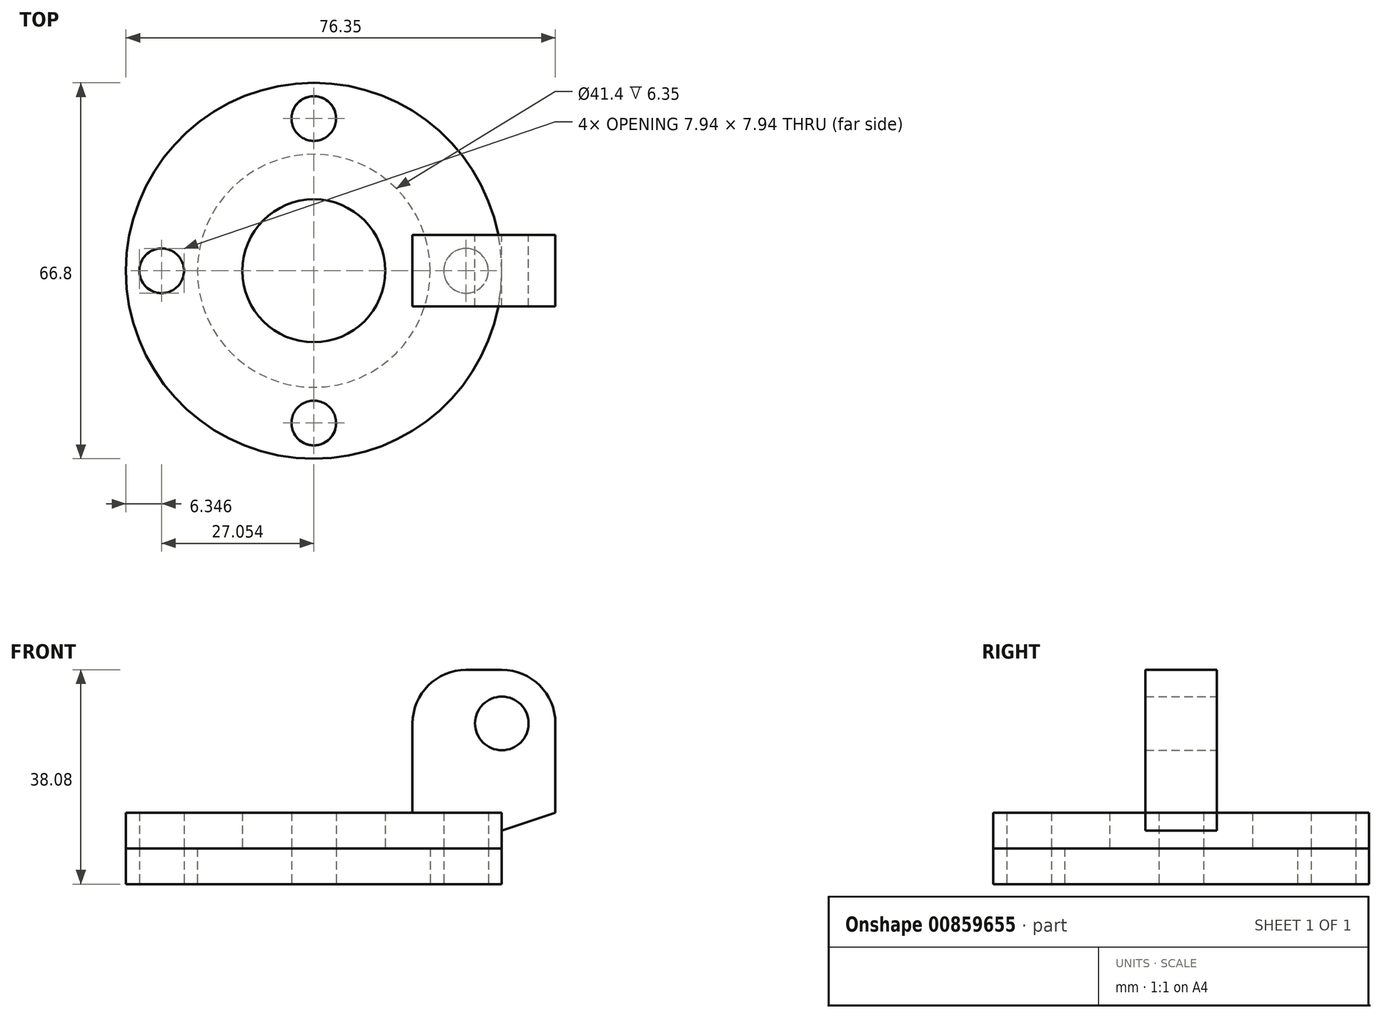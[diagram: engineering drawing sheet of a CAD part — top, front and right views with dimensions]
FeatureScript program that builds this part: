
annotation { "Feature Type Name" : "Feature", "Feature Type Description" : "" }
export const myFeature = defineFeature(function(context is Context, id is Id, definition is map)
    precondition{}
    {
        {
            var Q0;
            Q0=qCreatedBy(makeId("Top.planeOp"),FACE);
            var sketch = newSketch(context, id + "F0", { "sketchPlane" : qUnion([Q0])});
            skCircle(sketch, "E0", {"center": v(0, 0) * mm, "radius": 33.4 * mm});
            skCircle(sketch, "E1", {"center": v(0, 0) * mm, "radius": 20.7 * mm});
            skCircle(sketch, "E2", {"center": v(0, 27.05) * mm, "radius": 3.97 * mm});
            skCircle(sketch, "E3.1.0", {"center": v(-27.05, 0) * mm, "radius": 3.97 * mm});
            skCircle(sketch, "E3.2.0", {"center": v(0, -27.05) * mm, "radius": 3.97 * mm});
            skCircle(sketch, "E3.3.0", {"center": v(27.05, 0) * mm, "radius": 3.97 * mm});
            skSolve(sketch);
        }
        {
            var Q0;
            Q0=makeQuery(id+"F0.imprint","IMPRINT",FACE,{"disambiguationData":[TD([[makeQuery(id+"F0.imprint","IMPRINT",EDGE,{"derivedFrom":sQuery(id+"F0.wireOp",EDGE,"E0")}),1.0]])]});
            extrude(context, id + "F1", {"entities" : qUnion([Q0]), "endBound" : BoundingType.SYMMETRIC, "depth" : 6.35 * mm, "offsetDistance" : 25.4 * mm});
        }
        {
            var Q0;
            Q0=makeQuery(id+"F1.opExtrude","CAP_FACE",FACE,{"disambiguationData":[OSD([sQuery(id+"F0.wireOp",EDGE,"E0"),sQuery(id+"F0.wireOp",EDGE,"E1"),sQuery(id+"F0.wireOp",EDGE,"E2"),sQuery(id+"F0.wireOp",EDGE,"E3.1.0"),sQuery(id+"F0.wireOp",EDGE,"E3.2.0"),sQuery(id+"F0.wireOp",EDGE,"E3.3.0")])],"isStart":false});
            var Q1;
            Q1=qCreatedBy(makeId("Front.planeOp"),FACE);
            var Q2;
            Q2=qCreatedBy(makeId("Top.planeOp"),FACE);
            var sketch = newSketch(context, id + "F2", { "sketchPlane" : qUnion([Q0, Q1, Q2])});
            skCircle(sketch, "E4", {"center": v(0, 0) * mm, "radius": 33.4 * mm});
            skCircle(sketch, "E5", {"center": v(0, 0) * mm, "radius": 12.7 * mm});
            skCircle(sketch, "E6", {"center": v(0, 27.06) * mm, "radius": 3.97 * mm});
            skCircle(sketch, "E7", {"center": v(27.06, 0) * mm, "radius": 3.97 * mm});
            skCircle(sketch, "E8", {"center": v(0, -27.06) * mm, "radius": 3.97 * mm});
            skCircle(sketch, "E9", {"center": v(-27.06, 0) * mm, "radius": 3.97 * mm});
            skSolve(sketch);
        }
        {
            var Q0;
            Q0=makeQuery(id+"F2.imprint","IMPRINT",FACE,{"disambiguationData":[TD([[makeQuery(id+"F2.imprint","IMPRINT",EDGE,{"derivedFrom":sQuery(id+"F2.wireOp",EDGE,"E5")}),-1.0]])]});
            var Q1;
            Q1=makeQuery(id+"F2.imprint","IMPRINT",FACE,{"disambiguationData":[TD([[makeQuery(id+"F2.imprint","IMPRINT",EDGE,{"derivedFrom":makeQuery(id+"F1.opExtrude","CAP_EDGE",EDGE,{"disambiguationData":[OSD([sQuery(id+"F0.wireOp",EDGE,"E0")])],"isStart":false})}),1.0]])]});
            extrude(context, id + "F3", {"entities" : qUnion([Q0, Q1]), "depth" : 6.35 * mm, "offsetDistance" : 25.4 * mm});
        }
        {
            var Q0;
            Q0=qCreatedBy(makeId("Front.planeOp"),FACE);
            var sketch = newSketch(context, id + "F4", { "sketchPlane" : qUnion([Q0])});
            skLineSegment(sketch, "E10.bottom", {"start": v(43.32, 9.5) * mm, "end": v(42.95, 9.5) * mm});
            skLineSegment(sketch, "E10.top", {"start": v(33.43, 34.9) * mm, "end": v(27.08, 34.9) * mm});
            skLineSegment(sketch, "E10.left", {"start": v(42.95, 9.5) * mm, "end": v(42.95, 25.37) * mm});
            skLineSegment(sketch, "E10.right", {"start": v(17.55, 9.5) * mm, "end": v(17.55, 25.37) * mm});
            skPoint(sketch, "E10.middle", {"position": v(30.25, 22.2) * mm});
            skLineSegment(sketch, "E11", {"start": v(33.43, 34.45) * mm, "end": v(33.43, 5.76) * mm, "construction": true});
            skLineSegment(sketch, "E12.left", {"start": v(33.43, 9.5) * mm, "end": v(33.43, 6.32) * mm});
            skLineSegment(sketch, "E13.trimOffspring", {"start": v(33.43, 9.5) * mm, "end": v(17.55, 9.5) * mm});
            skCircle(sketch, "E14", {"center": v(33.43, 25.37) * mm, "radius": 4.76 * mm});
            skPoint(sketch, "E15.visualSharp", {"position": v(42.95, 34.9) * mm});
            skArc(sketch, "E15.filletArc", {"start": v(42.95, 25.37) * mm, "mid": v(40.16, 32.1) * mm, "end": v(33.43, 34.9) * mm});
            skPoint(sketch, "E16.visualSharp", {"position": v(17.55, 34.9) * mm});
            skArc(sketch, "E16.filletArc", {"start": v(27.08, 34.9) * mm, "mid": v(20.34, 32.1) * mm, "end": v(17.55, 25.37) * mm});
            skLineSegment(sketch, "E17", {"start": v(33.43, 6.32) * mm, "end": v(42.95, 9.5) * mm});
            skSolve(sketch);
        }
        {
            var Q0;
            Q0=makeQuery(id+"F4.imprint","IMPRINT",FACE,{"disambiguationData":[TD([[makeQuery(id+"F4.imprint","IMPRINT",EDGE,{"derivedFrom":sQuery(id+"F4.wireOp",EDGE,"E10.top")}),1.0]])]});
            extrude(context, id + "F5", {"entities" : qUnion([Q0]), "endBound" : BoundingType.SYMMETRIC, "depth" : 12.7 * mm, "offsetDistance" : 25.4 * mm});
        }
    });
